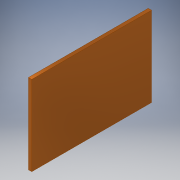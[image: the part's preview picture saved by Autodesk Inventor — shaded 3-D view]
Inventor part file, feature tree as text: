
AUTODESK INVENTOR PART (.ipt)
format: ipt  version: 2017 (Build 210142000, 142)  size: 89,600 bytes
history: native  units: in
note: dims shown in document units (in); Inventor stores cm internally (conversion verified against a paired STEP export)
features: extrude x1, sketch x1
ambient origin geometry x8: Origin, YZ Plane, XZ Plane, XY Plane, X Axis, Y Axis, Z Axis, Center Point
bodies: Solid1 (feature_tree)
feature tree (2):
  extrude  "Extrusion1"  Depth=36.0in
  sketch  "Sketch1"  dims[d0=24.0in d1=36.0in d2=1.0in d3=0.0in]
